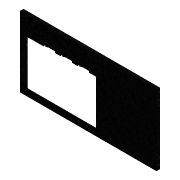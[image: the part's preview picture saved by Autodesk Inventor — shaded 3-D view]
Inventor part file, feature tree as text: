
AUTODESK INVENTOR PART (.ipt)
format: ipt  version: 2019.4 (Build 234330000, 330)  size: 197,120 bytes
history: native  units: mm
features: extrude x4, sketch x3, projected_geometry x2, other x2, hole x1, fillet x1, pattern_linear x1, reference x1
ambient origin geometry x8: Origin, YZ Plane, XZ Plane, XY Plane, X Axis, Y Axis, Z Axis, Center Point
bodies: Solid1 (feature_tree)
feature tree (15):
  extrude  "Extrusion1"  Depth=7.0mm
  extrude  "Extrusion7"  TaperAngle=0.0deg  [1 undecoded]
  hole  "Hole5"  [1 undecoded]
  fillet  "Fillet2"  Radius=6.0mm
  extrude  "Extrusion9"  Depth=2.0mm
  pattern_linear  "Rectangular Pattern2"  Spacing1=1.5mm  [1 undecoded]
  extrude  "Extrusion10"  Depth=1.5mm
  sketch  "Sketch1"  dims[d1=2.0mm d2=0.0mm d73=7.0mm]
  projected_geometry  "Projected Loop10"
  sketch  "Sketch12"  dims[d74=4.0mm d75=0.0mm d78=0.0mm]
  projected_geometry  "Projected Loop11"
  sketch  "Sketch13"  dims[d79=4.3mm d80=6.0mm d81=4.0mm d82=2.0mm d83=90.0deg d84=8.0mm d85=20.594885mm d86=5.0mm d87=6.0mm d88=2.0mm d89=1.5mm d90=1.5mm d91=27.925268mm d92=3.0mm d93=0.0mm d94=30.0mm d96=30.0mm d97=3.0mm d98=0.0mm]
  reference  "Reference34"
  other  "Assembly_Opentrons_Imagingunit_v3.iam"
  other  "00_MTP_96-welplate:1"
note: 3 required parameter values undecoded (feature->parameter linkage not recoverable at this tier; creation-order binding heuristic only, values carry confidence <= 0.55)
